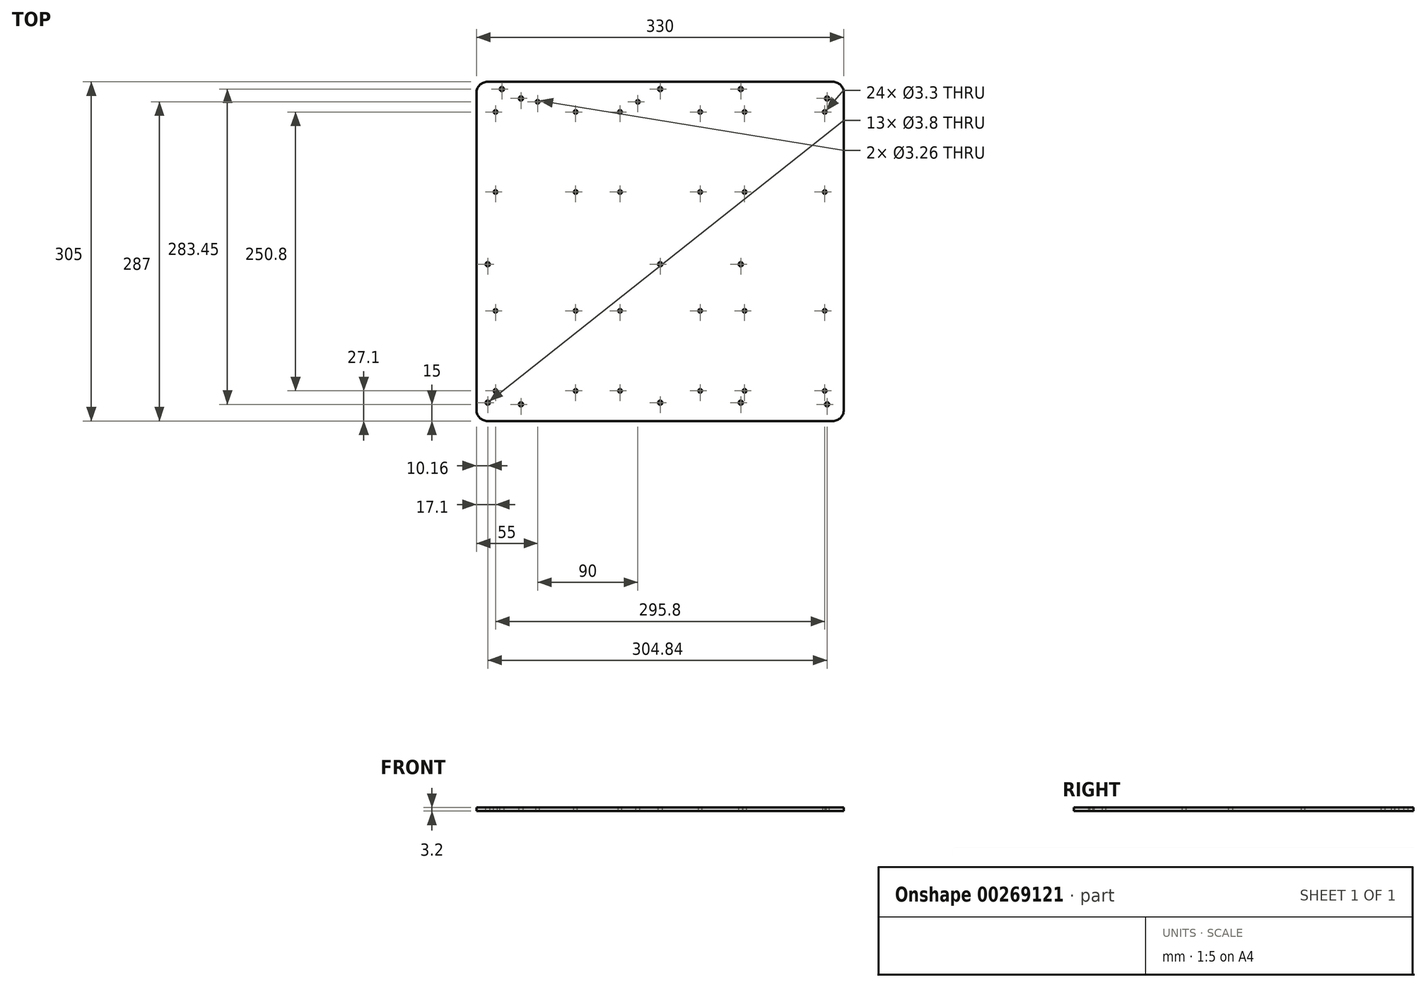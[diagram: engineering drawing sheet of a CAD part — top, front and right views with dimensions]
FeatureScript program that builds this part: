
annotation { "Feature Type Name" : "Feature", "Feature Type Description" : "" }
export const myFeature = defineFeature(function(context is Context, id is Id, definition is map)
    precondition{}
    {
        {
            var Q0;
            Q0=qCreatedBy(makeId("Top.planeOp"),FACE);
            var sketch = newSketch(context, id + "F0", { "sketchPlane" : qUnion([Q0])});
            skLineSegment(sketch, "E0.bottom", {"start": v(155, 147.5) * mm, "end": v(-155, 147.5) * mm});
            skLineSegment(sketch, "E0.top", {"start": v(155, -157.5) * mm, "end": v(-155, -157.5) * mm});
            skLineSegment(sketch, "E0.left", {"start": v(165, 137.5) * mm, "end": v(165, -147.5) * mm});
            skLineSegment(sketch, "E0.right", {"start": v(-165, 137.5) * mm, "end": v(-165, -147.5) * mm});
            skPoint(sketch, "E1.visualSharp", {"position": v(-165, 147.5) * mm});
            skArc(sketch, "E1.filletArc", {"start": v(-155, 147.5) * mm, "mid": v(-162.07, 144.57) * mm, "end": v(-165, 137.5) * mm});
            skPoint(sketch, "E2.visualSharp", {"position": v(165, 147.5) * mm});
            skArc(sketch, "E2.filletArc", {"start": v(165, 137.5) * mm, "mid": v(162.07, 144.57) * mm, "end": v(155, 147.5) * mm});
            skPoint(sketch, "E3.visualSharp", {"position": v(165, -157.5) * mm});
            skArc(sketch, "E3.filletArc", {"start": v(155, -157.5) * mm, "mid": v(162.07, -154.57) * mm, "end": v(165, -147.5) * mm});
            skPoint(sketch, "E4.visualSharp", {"position": v(-165, -157.5) * mm});
            skArc(sketch, "E4.filletArc", {"start": v(-165, -147.5) * mm, "mid": v(-162.07, -154.57) * mm, "end": v(-155, -157.5) * mm});
            skSolve(sketch);
        }
        {
            var Q0;
            Q0=makeQuery(id+"F0.imprint","IMPRINT",FACE,{"disambiguationData":[TD([[makeQuery(id+"F0.imprint","IMPRINT",EDGE,{"derivedFrom":sQuery(id+"F0.wireOp",EDGE,"E0.bottom")}),1.0]])]});
            extrude(context, id + "F1", {"entities" : qUnion([Q0]), "depth" : 3.2 * mm});
        }
        {
            var Q0;
            Q0=makeQuery(id+"F1.opExtrude","CAP_FACE",FACE,{"disambiguationData":[OSD([sQuery(id+"F0.wireOp",EDGE,"E0.bottom"),sQuery(id+"F0.wireOp",EDGE,"E0.top"),sQuery(id+"F0.wireOp",EDGE,"E0.left"),sQuery(id+"F0.wireOp",EDGE,"E0.right")])],"isStart":false});
            var sketch = newSketch(context, id + "F2", { "sketchPlane" : qUnion([Q0])});
            skPoint(sketch, "E5", {"position": v(-125, 132.5) * mm});
            skPoint(sketch, "E6", {"position": v(150, 132.5) * mm});
            skPoint(sketch, "E7", {"position": v(150, -142.5) * mm});
            skPoint(sketch, "E8", {"position": v(-125, -142.5) * mm});
            skSolve(sketch);
        }
        {
            var Q0;
            Q0=sQuery(id+"F2.wireOp",VERTEX,"E5");
            var Q1;
            Q1=sQuery(id+"F2.wireOp",VERTEX,"E6");
            var Q2;
            Q2=sQuery(id+"F2.wireOp",VERTEX,"E7");
            var Q3;
            Q3=sQuery(id+"F2.wireOp",VERTEX,"E8");
            var Q4;
            Q4=makeQuery(id+"F1.opExtrude","SWEPT_BODY",BODY,{"disambiguationData":[OSD([sQuery(id+"F0.wireOp",EDGE,"E0.bottom"),sQuery(id+"F0.wireOp",EDGE,"E0.top"),sQuery(id+"F0.wireOp",EDGE,"E0.left"),sQuery(id+"F0.wireOp",EDGE,"E0.right")])]});
            hole(context, id + "F3", {"style" : HoleStyle.SIMPLE, "endStyle" : HoleEndStyle.THROUGH, "standardTappedOrClearance" : lookupTablePath({ "standard" : "ANSI", "fit" : "Normal (ASME)", "size" : "#6", "type" : "Clearance" }), "standardBlindInLast" : lookupTablePath({ "fit" : "Free", "standard" : "ANSI", "size" : "#6", "type" : "Clearance" }), "holeDiameter" : 3.8 * mm, "tappedDepth" : 12 * mm, "tapClearance" : 3, "locations" : qUnion([Q0, Q1, Q2, Q3]), "scope" : qUnion([Q4])});
        }
        {
            var Q0;
            Q0=makeQuery(id+"F1.opExtrude","CAP_FACE",FACE,{"disambiguationData":[OSD([sQuery(id+"F0.wireOp",EDGE,"E0.bottom"),sQuery(id+"F0.wireOp",EDGE,"E0.top"),sQuery(id+"F0.wireOp",EDGE,"E0.left"),sQuery(id+"F0.wireOp",EDGE,"E0.right")])],"isStart":false});
            var sketch = newSketch(context, id + "F4", { "sketchPlane" : qUnion([Q0])});
            skPoint(sketch, "E9", {"position": v(-142.14, 140.95) * mm});
            skPoint(sketch, "E10", {"position": v(0.1, 140.95) * mm});
            skPoint(sketch, "E11", {"position": v(72.5, 140.95) * mm});
            skPoint(sketch, "E12", {"position": v(-154.84, -16.53) * mm});
            skPoint(sketch, "E13", {"position": v(0.1, -16.53) * mm});
            skPoint(sketch, "E14", {"position": v(72.5, -16.53) * mm});
            skPoint(sketch, "E15", {"position": v(72.5, -140.99) * mm});
            skPoint(sketch, "E16", {"position": v(0.1, -140.99) * mm});
            skPoint(sketch, "E17", {"position": v(-154.84, -140.99) * mm});
            skSolve(sketch);
        }
        {
            var Q0;
            Q0=sQuery(id+"F4.wireOp",VERTEX,"E9");
            var Q1;
            Q1=sQuery(id+"F4.wireOp",VERTEX,"E10");
            var Q2;
            Q2=sQuery(id+"F4.wireOp",VERTEX,"E11");
            var Q3;
            Q3=sQuery(id+"F4.wireOp",VERTEX,"E12");
            var Q4;
            Q4=sQuery(id+"F4.wireOp",VERTEX,"E13");
            var Q5;
            Q5=sQuery(id+"F4.wireOp",VERTEX,"E14");
            var Q6;
            Q6=sQuery(id+"F4.wireOp",VERTEX,"E15");
            var Q7;
            Q7=sQuery(id+"F4.wireOp",VERTEX,"E16");
            var Q8;
            Q8=sQuery(id+"F4.wireOp",VERTEX,"E17");
            var Q9;
            Q9=makeQuery(id+"F1.opExtrude","SWEPT_BODY",BODY,{"disambiguationData":[OSD([sQuery(id+"F0.wireOp",EDGE,"E0.bottom"),sQuery(id+"F0.wireOp",EDGE,"E0.top"),sQuery(id+"F0.wireOp",EDGE,"E0.left"),sQuery(id+"F0.wireOp",EDGE,"E0.right")])]});
            hole(context, id + "F5", {"style" : HoleStyle.SIMPLE, "endStyle" : HoleEndStyle.THROUGH, "standardTappedOrClearance" : lookupTablePath({ "standard" : "ANSI", "fit" : "Normal (ASME)", "size" : "#6", "type" : "Clearance" }), "standardBlindInLast" : lookupTablePath({ "fit" : "Free", "standard" : "ANSI", "size" : "#6", "type" : "Clearance" }), "holeDiameter" : 3.8 * mm, "tappedDepth" : 12 * mm, "tapClearance" : 3, "locations" : qUnion([Q0, Q1, Q2, Q3, Q4, Q5, Q6, Q7, Q8]), "scope" : qUnion([Q9])});
        }
        {
            var Q0;
            Q0=makeQuery(id+"F1.opExtrude","CAP_FACE",FACE,{"disambiguationData":[OSD([sQuery(id+"F0.wireOp",EDGE,"E0.bottom"),sQuery(id+"F0.wireOp",EDGE,"E0.top"),sQuery(id+"F0.wireOp",EDGE,"E0.left"),sQuery(id+"F0.wireOp",EDGE,"E0.right")])],"isStart":false});
            var sketch = newSketch(context, id + "F6", { "sketchPlane" : qUnion([Q0])});
            skPoint(sketch, "E18", {"position": v(-147.9, 120.4) * mm});
            skPoint(sketch, "E19", {"position": v(-75.9, 120.4) * mm});
            skPoint(sketch, "E20", {"position": v(-75.9, 48.4) * mm});
            skPoint(sketch, "E21", {"position": v(-147.9, 48.4) * mm});
            skLineSegment(sketch, "E22.bottom", {"start": v(-150, 122.5) * mm, "end": v(-73.8, 122.5) * mm});
            skLineSegment(sketch, "E22.top", {"start": v(-150, 46.3) * mm, "end": v(-73.8, 46.3) * mm});
            skLineSegment(sketch, "E22.left", {"start": v(-150, 122.5) * mm, "end": v(-150, 46.3) * mm});
            skLineSegment(sketch, "E22.right", {"start": v(-73.8, 122.5) * mm, "end": v(-73.8, 46.3) * mm});
            skLineSegment(sketch, "E23", {"start": v(-147.9, 120.4) * mm, "end": v(-147.9, 122.5) * mm});
            skLineSegment(sketch, "E24", {"start": v(-147.9, 122.5) * mm, "end": v(-147.9, 120.4) * mm});
            skLineSegment(sketch, "E25", {"start": v(-150, 120.4) * mm, "end": v(-147.9, 120.4) * mm});
            skLineSegment(sketch, "E26", {"start": v(-75.9, 120.4) * mm, "end": v(-73.8, 120.4) * mm});
            skLineSegment(sketch, "E27", {"start": v(-73.8, 120.4) * mm, "end": v(-75.9, 120.4) * mm});
            skLineSegment(sketch, "E28", {"start": v(-75.9, 120.4) * mm, "end": v(-75.9, 122.5) * mm});
            skLineSegment(sketch, "E29", {"start": v(-75.9, 48.4) * mm, "end": v(-73.8, 48.4) * mm});
            skLineSegment(sketch, "E30", {"start": v(-75.9, 48.4) * mm, "end": v(-75.9, 46.3) * mm});
            skLineSegment(sketch, "E31", {"start": v(-147.9, 48.4) * mm, "end": v(-150, 48.4) * mm});
            skLineSegment(sketch, "E32", {"start": v(-147.9, 48.4) * mm, "end": v(-147.9, 46.3) * mm});
            skPoint(sketch, "E33.0.1.0", {"position": v(-147.9, -130.4) * mm});
            skPoint(sketch, "E33.0.1.1", {"position": v(-75.9, -130.4) * mm});
            skPoint(sketch, "E33.0.1.2", {"position": v(-147.9, -58.4) * mm});
            skPoint(sketch, "E33.0.1.3", {"position": v(-75.9, -58.4) * mm});
            skLineSegment(sketch, "E33.0.1.4", {"start": v(-73.8, -56.3) * mm, "end": v(-73.8, -132.5) * mm});
            skLineSegment(sketch, "E33.0.1.5", {"start": v(-150, -56.3) * mm, "end": v(-150, -132.5) * mm});
            skLineSegment(sketch, "E33.0.1.6", {"start": v(-150, -132.5) * mm, "end": v(-73.8, -132.5) * mm});
            skLineSegment(sketch, "E33.0.1.7", {"start": v(-150, -56.3) * mm, "end": v(-73.8, -56.3) * mm});
            skLineSegment(sketch, "E33.0.1.8", {"start": v(-147.9, -130.4) * mm, "end": v(-150, -130.4) * mm});
            skLineSegment(sketch, "E33.0.1.9", {"start": v(-75.9, -130.4) * mm, "end": v(-75.9, -132.5) * mm});
            skLineSegment(sketch, "E33.0.1.10", {"start": v(-75.9, -130.4) * mm, "end": v(-73.8, -130.4) * mm});
            skLineSegment(sketch, "E33.0.1.11", {"start": v(-147.9, -130.4) * mm, "end": v(-147.9, -132.5) * mm});
            skLineSegment(sketch, "E33.0.1.12", {"start": v(-75.9, -58.4) * mm, "end": v(-75.9, -56.3) * mm});
            skLineSegment(sketch, "E33.0.1.13", {"start": v(-73.8, -58.4) * mm, "end": v(-75.9, -58.4) * mm});
            skLineSegment(sketch, "E33.0.1.14", {"start": v(-150, -58.4) * mm, "end": v(-147.9, -58.4) * mm});
            skLineSegment(sketch, "E33.0.1.15", {"start": v(-147.9, -56.3) * mm, "end": v(-147.9, -58.4) * mm});
            skLineSegment(sketch, "E33.0.1.16", {"start": v(-75.9, -58.4) * mm, "end": v(-73.8, -58.4) * mm});
            skLineSegment(sketch, "E33.0.1.17", {"start": v(-147.9, -58.4) * mm, "end": v(-147.9, -56.3) * mm});
            skPoint(sketch, "E33.1.0.0", {"position": v(-36, 48.4) * mm});
            skPoint(sketch, "E33.1.0.1", {"position": v(36, 48.4) * mm});
            skPoint(sketch, "E33.1.0.2", {"position": v(-36, 120.4) * mm});
            skPoint(sketch, "E33.1.0.3", {"position": v(36, 120.4) * mm});
            skLineSegment(sketch, "E33.1.0.4", {"start": v(38.1, 122.5) * mm, "end": v(38.1, 46.3) * mm});
            skLineSegment(sketch, "E33.1.0.5", {"start": v(-38.1, 122.5) * mm, "end": v(-38.1, 46.3) * mm});
            skLineSegment(sketch, "E33.1.0.6", {"start": v(-38.1, 46.3) * mm, "end": v(38.1, 46.3) * mm});
            skLineSegment(sketch, "E33.1.0.7", {"start": v(-38.1, 122.5) * mm, "end": v(38.1, 122.5) * mm});
            skLineSegment(sketch, "E33.1.0.8", {"start": v(-36, 48.4) * mm, "end": v(-38.1, 48.4) * mm});
            skLineSegment(sketch, "E33.1.0.9", {"start": v(36, 48.4) * mm, "end": v(36, 46.3) * mm});
            skLineSegment(sketch, "E33.1.0.10", {"start": v(36, 48.4) * mm, "end": v(38.1, 48.4) * mm});
            skLineSegment(sketch, "E33.1.0.11", {"start": v(-36, 48.4) * mm, "end": v(-36, 46.3) * mm});
            skLineSegment(sketch, "E33.1.0.12", {"start": v(36, 120.4) * mm, "end": v(36, 122.5) * mm});
            skLineSegment(sketch, "E33.1.0.13", {"start": v(38.1, 120.4) * mm, "end": v(36, 120.4) * mm});
            skLineSegment(sketch, "E33.1.0.14", {"start": v(-38.1, 120.4) * mm, "end": v(-36, 120.4) * mm});
            skLineSegment(sketch, "E33.1.0.15", {"start": v(-36, 122.5) * mm, "end": v(-36, 120.4) * mm});
            skLineSegment(sketch, "E33.1.0.16", {"start": v(36, 120.4) * mm, "end": v(38.1, 120.4) * mm});
            skLineSegment(sketch, "E33.1.0.17", {"start": v(-36, 120.4) * mm, "end": v(-36, 122.5) * mm});
            skPoint(sketch, "E33.1.1.0", {"position": v(-36, -130.4) * mm});
            skPoint(sketch, "E33.1.1.1", {"position": v(36, -130.4) * mm});
            skPoint(sketch, "E33.1.1.2", {"position": v(-36, -58.4) * mm});
            skPoint(sketch, "E33.1.1.3", {"position": v(36, -58.4) * mm});
            skLineSegment(sketch, "E33.1.1.4", {"start": v(38.1, -56.3) * mm, "end": v(38.1, -132.5) * mm});
            skLineSegment(sketch, "E33.1.1.5", {"start": v(-38.1, -56.3) * mm, "end": v(-38.1, -132.5) * mm});
            skLineSegment(sketch, "E33.1.1.6", {"start": v(-38.1, -132.5) * mm, "end": v(38.1, -132.5) * mm});
            skLineSegment(sketch, "E33.1.1.7", {"start": v(-38.1, -56.3) * mm, "end": v(38.1, -56.3) * mm});
            skLineSegment(sketch, "E33.1.1.8", {"start": v(-36, -130.4) * mm, "end": v(-38.1, -130.4) * mm});
            skLineSegment(sketch, "E33.1.1.9", {"start": v(36, -130.4) * mm, "end": v(36, -132.5) * mm});
            skLineSegment(sketch, "E33.1.1.10", {"start": v(36, -130.4) * mm, "end": v(38.1, -130.4) * mm});
            skLineSegment(sketch, "E33.1.1.11", {"start": v(-36, -130.4) * mm, "end": v(-36, -132.5) * mm});
            skLineSegment(sketch, "E33.1.1.12", {"start": v(36, -58.4) * mm, "end": v(36, -56.3) * mm});
            skLineSegment(sketch, "E33.1.1.13", {"start": v(38.1, -58.4) * mm, "end": v(36, -58.4) * mm});
            skLineSegment(sketch, "E33.1.1.14", {"start": v(-38.1, -58.4) * mm, "end": v(-36, -58.4) * mm});
            skLineSegment(sketch, "E33.1.1.15", {"start": v(-36, -56.3) * mm, "end": v(-36, -58.4) * mm});
            skLineSegment(sketch, "E33.1.1.16", {"start": v(36, -58.4) * mm, "end": v(38.1, -58.4) * mm});
            skLineSegment(sketch, "E33.1.1.17", {"start": v(-36, -58.4) * mm, "end": v(-36, -56.3) * mm});
            skPoint(sketch, "E33.2.0.0", {"position": v(75.9, 48.4) * mm});
            skPoint(sketch, "E33.2.0.1", {"position": v(147.9, 48.4) * mm});
            skPoint(sketch, "E33.2.0.2", {"position": v(75.9, 120.4) * mm});
            skPoint(sketch, "E33.2.0.3", {"position": v(147.9, 120.4) * mm});
            skLineSegment(sketch, "E33.2.0.4", {"start": v(150, 122.5) * mm, "end": v(150, 46.3) * mm});
            skLineSegment(sketch, "E33.2.0.5", {"start": v(73.8, 122.5) * mm, "end": v(73.8, 46.3) * mm});
            skLineSegment(sketch, "E33.2.0.6", {"start": v(73.8, 46.3) * mm, "end": v(150, 46.3) * mm});
            skLineSegment(sketch, "E33.2.0.7", {"start": v(73.8, 122.5) * mm, "end": v(150, 122.5) * mm});
            skLineSegment(sketch, "E33.2.0.8", {"start": v(75.9, 48.4) * mm, "end": v(73.8, 48.4) * mm});
            skLineSegment(sketch, "E33.2.0.9", {"start": v(147.9, 48.4) * mm, "end": v(147.9, 46.3) * mm});
            skLineSegment(sketch, "E33.2.0.10", {"start": v(147.9, 48.4) * mm, "end": v(150, 48.4) * mm});
            skLineSegment(sketch, "E33.2.0.11", {"start": v(75.9, 48.4) * mm, "end": v(75.9, 46.3) * mm});
            skLineSegment(sketch, "E33.2.0.12", {"start": v(147.9, 120.4) * mm, "end": v(147.9, 122.5) * mm});
            skLineSegment(sketch, "E33.2.0.13", {"start": v(150, 120.4) * mm, "end": v(147.9, 120.4) * mm});
            skLineSegment(sketch, "E33.2.0.14", {"start": v(73.8, 120.4) * mm, "end": v(75.9, 120.4) * mm});
            skLineSegment(sketch, "E33.2.0.15", {"start": v(75.9, 122.5) * mm, "end": v(75.9, 120.4) * mm});
            skLineSegment(sketch, "E33.2.0.16", {"start": v(147.9, 120.4) * mm, "end": v(150, 120.4) * mm});
            skLineSegment(sketch, "E33.2.0.17", {"start": v(75.9, 120.4) * mm, "end": v(75.9, 122.5) * mm});
            skPoint(sketch, "E33.2.1.0", {"position": v(75.9, -130.4) * mm});
            skPoint(sketch, "E33.2.1.1", {"position": v(147.9, -130.4) * mm});
            skPoint(sketch, "E33.2.1.2", {"position": v(75.9, -58.4) * mm});
            skPoint(sketch, "E33.2.1.3", {"position": v(147.9, -58.4) * mm});
            skLineSegment(sketch, "E33.2.1.4", {"start": v(150, -56.3) * mm, "end": v(150, -132.5) * mm});
            skLineSegment(sketch, "E33.2.1.5", {"start": v(73.8, -56.3) * mm, "end": v(73.8, -132.5) * mm});
            skLineSegment(sketch, "E33.2.1.6", {"start": v(73.8, -132.5) * mm, "end": v(150, -132.5) * mm});
            skLineSegment(sketch, "E33.2.1.7", {"start": v(73.8, -56.3) * mm, "end": v(150, -56.3) * mm});
            skLineSegment(sketch, "E33.2.1.8", {"start": v(75.9, -130.4) * mm, "end": v(73.8, -130.4) * mm});
            skLineSegment(sketch, "E33.2.1.9", {"start": v(147.9, -130.4) * mm, "end": v(147.9, -132.5) * mm});
            skLineSegment(sketch, "E33.2.1.10", {"start": v(147.9, -130.4) * mm, "end": v(150, -130.4) * mm});
            skLineSegment(sketch, "E33.2.1.11", {"start": v(75.9, -130.4) * mm, "end": v(75.9, -132.5) * mm});
            skLineSegment(sketch, "E33.2.1.12", {"start": v(147.9, -58.4) * mm, "end": v(147.9, -56.3) * mm});
            skLineSegment(sketch, "E33.2.1.13", {"start": v(150, -58.4) * mm, "end": v(147.9, -58.4) * mm});
            skLineSegment(sketch, "E33.2.1.14", {"start": v(73.8, -58.4) * mm, "end": v(75.9, -58.4) * mm});
            skLineSegment(sketch, "E33.2.1.15", {"start": v(75.9, -56.3) * mm, "end": v(75.9, -58.4) * mm});
            skLineSegment(sketch, "E33.2.1.16", {"start": v(147.9, -58.4) * mm, "end": v(150, -58.4) * mm});
            skLineSegment(sketch, "E33.2.1.17", {"start": v(75.9, -58.4) * mm, "end": v(75.9, -56.3) * mm});
            skLineSegment(sketch, "E33.direction1", {"start": v(-150, 46.3) * mm, "end": v(-38.1, 46.3) * mm, "construction": true});
            skLineSegment(sketch, "E33.direction2", {"start": v(-150, 46.3) * mm, "end": v(-150, -132.5) * mm, "construction": true});
            skPoint(sketch, "E34", {"position": v(-135, 31.3) * mm});
            skPoint(sketch, "E35", {"position": v(-23.1, 31.3) * mm});
            skPoint(sketch, "E36", {"position": v(88.8, 31.3) * mm});
            skPoint(sketch, "E37", {"position": v(23.1, -41.3) * mm});
            skPoint(sketch, "E38", {"position": v(135, -41.3) * mm});
            skPoint(sketch, "E39", {"position": v(-88.8, -41.3) * mm});
            skSolve(sketch);
        }
        {
            var Q0;
            Q0=sQuery(id+"F6.wireOp",VERTEX,"E18");
            var Q1;
            Q1=sQuery(id+"F6.wireOp",VERTEX,"E19");
            var Q2;
            Q2=sQuery(id+"F6.wireOp",VERTEX,"E21");
            var Q3;
            Q3=sQuery(id+"F6.wireOp",VERTEX,"E20");
            var Q4;
            Q4=sQuery(id+"F6.wireOp",VERTEX,"E33.1.0.2");
            var Q5;
            Q5=sQuery(id+"F6.wireOp",VERTEX,"E33.1.0.3");
            var Q6;
            Q6=sQuery(id+"F6.wireOp",VERTEX,"E33.1.0.0");
            var Q7;
            Q7=sQuery(id+"F6.wireOp",VERTEX,"E33.1.0.1");
            var Q8;
            Q8=sQuery(id+"F6.wireOp",VERTEX,"E33.2.0.2");
            var Q9;
            Q9=sQuery(id+"F6.wireOp",VERTEX,"E33.2.0.3");
            var Q10;
            Q10=sQuery(id+"F6.wireOp",VERTEX,"E33.2.0.0");
            var Q11;
            Q11=sQuery(id+"F6.wireOp",VERTEX,"E33.2.0.1");
            var Q12;
            Q12=sQuery(id+"F6.wireOp",VERTEX,"E33.0.1.0");
            var Q13;
            Q13=sQuery(id+"F6.wireOp",VERTEX,"E33.0.1.2");
            var Q14;
            Q14=sQuery(id+"F6.wireOp",VERTEX,"E33.0.1.3");
            var Q15;
            Q15=sQuery(id+"F6.wireOp",VERTEX,"E33.0.1.1");
            var Q16;
            Q16=sQuery(id+"F6.wireOp",VERTEX,"E33.1.1.2");
            var Q17;
            Q17=sQuery(id+"F6.wireOp",VERTEX,"E33.1.1.3");
            var Q18;
            Q18=sQuery(id+"F6.wireOp",VERTEX,"E33.1.1.0");
            var Q19;
            Q19=sQuery(id+"F6.wireOp",VERTEX,"E33.1.1.1");
            var Q20;
            Q20=sQuery(id+"F6.wireOp",VERTEX,"E33.2.1.2");
            var Q21;
            Q21=sQuery(id+"F6.wireOp",VERTEX,"E33.2.1.3");
            var Q22;
            Q22=sQuery(id+"F6.wireOp",VERTEX,"E33.2.1.0");
            var Q23;
            Q23=sQuery(id+"F6.wireOp",VERTEX,"E33.2.1.1");
            var Q24;
            Q24=makeQuery(id+"F1.opExtrude","SWEPT_BODY",BODY,{"disambiguationData":[OSD([sQuery(id+"F0.wireOp",EDGE,"E0.bottom"),sQuery(id+"F0.wireOp",EDGE,"E0.top"),sQuery(id+"F0.wireOp",EDGE,"E0.left"),sQuery(id+"F0.wireOp",EDGE,"E0.right")])]});
            hole(context, id + "F7", {"style" : HoleStyle.SIMPLE, "endStyle" : HoleEndStyle.THROUGH, "standardTappedOrClearance" : lookupTablePath({ "standard" : "ISO", "fit" : "Normal", "size" : "M3", "type" : "Clearance" }), "standardBlindInLast" : lookupTablePath({ "fit" : "Standard", "standard" : "ISO", "size" : "M3", "type" : "Clearance" }), "holeDiameter" : 3.3 * mm, "tappedDepth" : 12 * mm, "tapClearance" : 3, "locations" : qUnion([Q0, Q1, Q2, Q3, Q4, Q5, Q6, Q7, Q8, Q9, Q10, Q11, Q12, Q13, Q14, Q15, Q16, Q17, Q18, Q19, Q20, Q21, Q22, Q23]), "scope" : qUnion([Q24])});
        }
        {
            var Q0;
            Q0=makeQuery(id+"F6.imprint","IMPRINT",FACE,{"disambiguationData":[TD([[makeQuery(id+"F6.imprint","IMPRINT",EDGE,{"derivedFrom":makeQuery(id+"F1.opExtrude","CAP_EDGE",EDGE,{"disambiguationData":[OSD([sQuery(id+"F0.wireOp",EDGE,"E0.bottom")])],"isStart":false})}),1.0]])]});
            var sketch = newSketch(context, id + "F8", { "sketchPlane" : qUnion([Q0])});
            skPoint(sketch, "E40", {"position": v(-110, 129.5) * mm});
            skPoint(sketch, "E41", {"position": v(-20, 129.5) * mm});
            skSolve(sketch);
        }
        {
            var Q0;
            Q0=sQuery(id+"F8.wireOp",VERTEX,"E40");
            var Q1;
            Q1=sQuery(id+"F8.wireOp",VERTEX,"E41");
            var Q2;
            Q2=makeQuery(id+"F1.opExtrude","SWEPT_BODY",BODY,{"disambiguationData":[OSD([sQuery(id+"F0.wireOp",EDGE,"E0.bottom"),sQuery(id+"F0.wireOp",EDGE,"E0.top"),sQuery(id+"F0.wireOp",EDGE,"E0.left"),sQuery(id+"F0.wireOp",EDGE,"E0.right"),sQuery(id+"F0.wireOp",EDGE,"E1.filletArc"),sQuery(id+"F0.wireOp",EDGE,"E2.filletArc"),sQuery(id+"F0.wireOp",EDGE,"E3.filletArc"),sQuery(id+"F0.wireOp",EDGE,"E4.filletArc")])]});
            hole(context, id + "F9", {"style" : HoleStyle.SIMPLE, "endStyle" : HoleEndStyle.THROUGH, "standardTappedOrClearance" : lookupTablePath({ "standard" : "ANSI", "fit" : "Normal (ASME)", "size" : "#4", "type" : "Clearance" }), "standardBlindInLast" : lookupTablePath({ "fit" : "Free", "standard" : "ANSI", "size" : "#4", "type" : "Clearance" }), "holeDiameter" : 3.26 * mm, "tappedDepth" : 12 * mm, "tapClearance" : 3, "locations" : qUnion([Q0, Q1]), "scope" : qUnion([Q2])});
        }
    });
